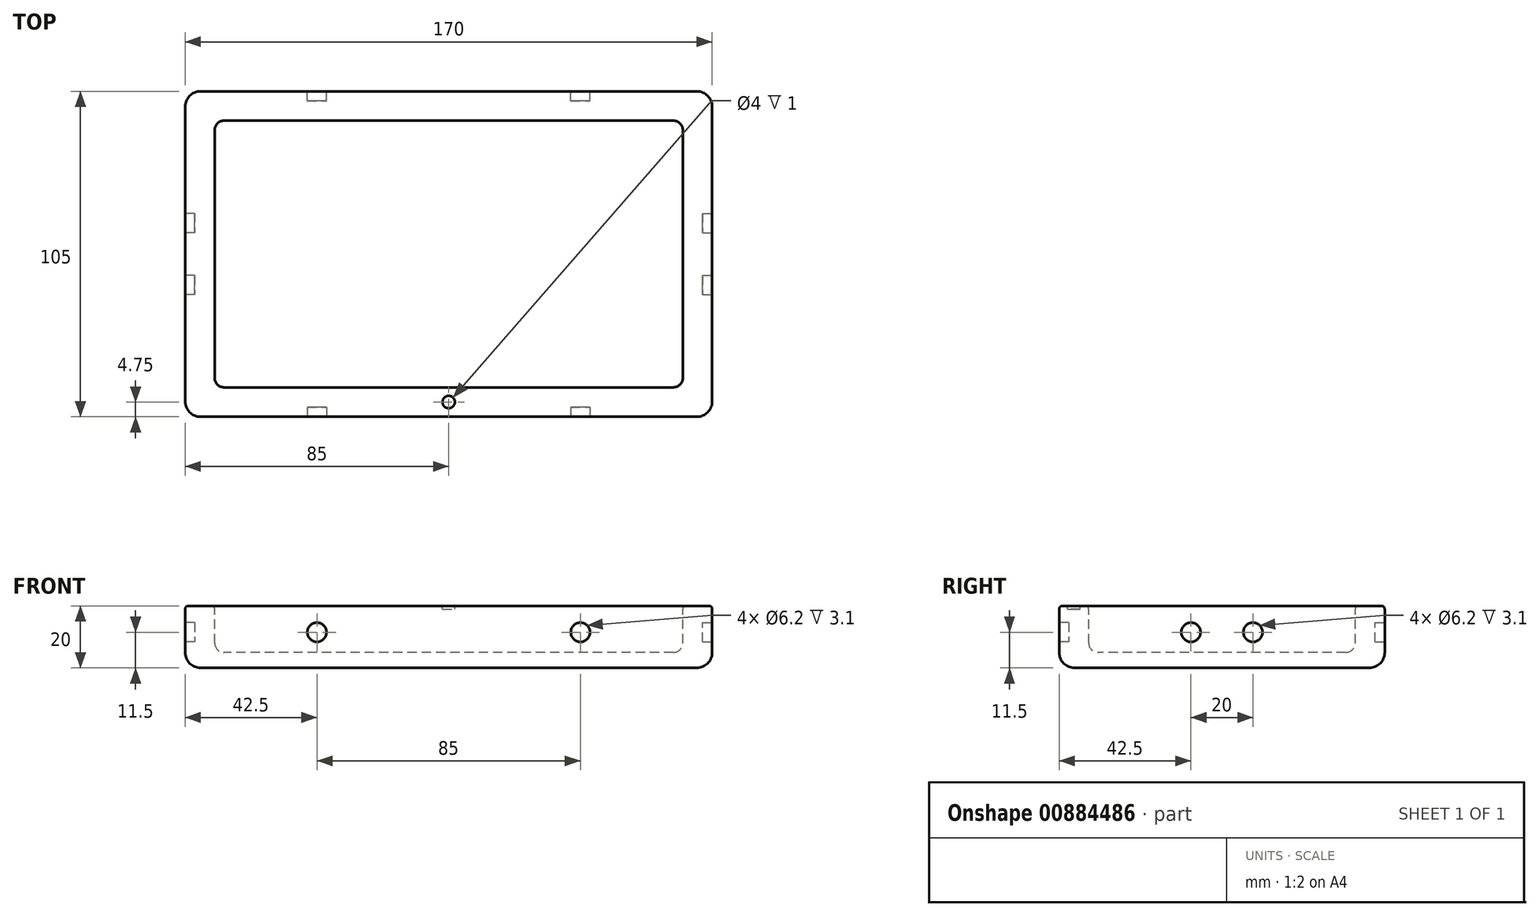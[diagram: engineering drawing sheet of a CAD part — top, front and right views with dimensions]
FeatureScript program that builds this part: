
annotation { "Feature Type Name" : "Feature", "Feature Type Description" : "" }
export const myFeature = defineFeature(function(context is Context, id is Id, definition is map)
    precondition{}
    {
        {
            var Q0;
            Q0=qCreatedBy(makeId("Top.planeOp"),FACE);
            var sketch = newSketch(context, id + "F0", { "sketchPlane" : qUnion([Q0])});
            skLineSegment(sketch, "E0.bottom", {"start": v(-85, 52.5) * mm, "end": v(85, 52.5) * mm});
            skLineSegment(sketch, "E0.top", {"start": v(-85, -52.5) * mm, "end": v(85, -52.5) * mm});
            skLineSegment(sketch, "E0.left", {"start": v(-85, 52.5) * mm, "end": v(-85, -52.5) * mm});
            skLineSegment(sketch, "E0.right", {"start": v(85, 52.5) * mm, "end": v(85, -52.5) * mm});
            skLineSegment(sketch, "E1.bottom", {"start": v(-72.5, 43) * mm, "end": v(72.5, 43) * mm});
            skLineSegment(sketch, "E1.top", {"start": v(-72.5, -43) * mm, "end": v(72.5, -43) * mm});
            skLineSegment(sketch, "E1.left", {"start": v(-75.5, 40) * mm, "end": v(-75.5, -40) * mm});
            skLineSegment(sketch, "E1.right", {"start": v(75.5, 40) * mm, "end": v(75.5, -40) * mm});
            skLineSegment(sketch, "E2.direction1", {"start": v(-75.5, -43) * mm, "end": v(15.26, -43) * mm, "construction": true});
            skPoint(sketch, "E3.visualSharp", {"position": v(-75.5, 43) * mm});
            skArc(sketch, "E3.filletArc", {"start": v(-72.5, 43) * mm, "mid": v(-74.62, 42.12) * mm, "end": v(-75.5, 40) * mm});
            skPoint(sketch, "E4.visualSharp", {"position": v(75.5, 43) * mm});
            skArc(sketch, "E4.filletArc", {"start": v(75.5, 40) * mm, "mid": v(74.62, 42.12) * mm, "end": v(72.5, 43) * mm});
            skPoint(sketch, "E5.visualSharp", {"position": v(75.5, -43) * mm});
            skArc(sketch, "E5.filletArc", {"start": v(72.5, -43) * mm, "mid": v(74.62, -42.12) * mm, "end": v(75.5, -40) * mm});
            skPoint(sketch, "E6.visualSharp", {"position": v(-75.5, -43) * mm});
            skArc(sketch, "E6.filletArc", {"start": v(-75.5, -40) * mm, "mid": v(-74.62, -42.12) * mm, "end": v(-72.5, -43) * mm});
            skLineSegment(sketch, "E7.direction1", {"start": v(-75.5, -43) * mm, "end": v(17, -43) * mm, "construction": true});
            skLineSegment(sketch, "E8", {"start": v(-85, 0) * mm, "end": v(85, 0) * mm, "construction": true});
            skLineSegment(sketch, "E9", {"start": v(0, -52.5) * mm, "end": v(0, 52.5) * mm, "construction": true});
            skCircle(sketch, "E10", {"center": v(0, -47.75) * mm, "radius": 2 * mm});
            skSolve(sketch);
        }
        {
            assignVariable(context, id + "F1", {"name" : "h", "anyValue" : 20});
        }
        {
            assignVariable(context, id + "F2", {"name" : "d", "anyValue" : 15});
        }
        {
            var Q0;
            Q0=makeQuery(id+"F0.imprint","IMPRINT",FACE,{"disambiguationData":[TD([[makeQuery(id+"F0.imprint","IMPRINT",EDGE,{"derivedFrom":sQuery(id+"F0.wireOp",EDGE,"E1.bottom")}),-1.0]])]});
            var Q1;
            Q1=makeQuery(id+"F0.imprint","IMPRINT",FACE,{"disambiguationData":[TD([[makeQuery(id+"F0.imprint","IMPRINT",EDGE,{"derivedFrom":sQuery(id+"F0.wireOp",EDGE,"E0.bottom")}),-1.0]])]});
            var Q2;
            Q2=makeQuery(id+"F0.imprint","IMPRINT",FACE,{"disambiguationData":[TD([[makeQuery(id+"F0.imprint","IMPRINT",EDGE,{"derivedFrom":sQuery(id+"F0.wireOp",EDGE,"E2.0.2.0")}),1.0]])]});
            var Q3;
            Q3=makeQuery(id+"F0.imprint","IMPRINT",FACE,{"disambiguationData":[TD([[makeQuery(id+"F0.imprint","IMPRINT",EDGE,{"derivedFrom":sQuery(id+"F0.wireOp",EDGE,"E2.0.3.0")}),1.0]])]});
            var Q4;
            Q4=makeQuery(id+"F0.imprint","IMPRINT",FACE,{"disambiguationData":[TD([[makeQuery(id+"F0.imprint","IMPRINT",EDGE,{"derivedFrom":sQuery(id+"F0.wireOp",EDGE,"E2.0.1.0")}),1.0]])]});
            var Q5;
            Q5=makeQuery(id+"F0.imprint","IMPRINT",FACE,{"disambiguationData":[TD([[makeQuery(id+"F0.imprint","IMPRINT",EDGE,{"derivedFrom":sQuery(id+"F0.wireOp",EDGE,"E7.0.1.2")}),1.0]])]});
            var Q6;
            Q6=makeQuery(id+"F0.imprint","IMPRINT",FACE,{"disambiguationData":[TD([[makeQuery(id+"F0.imprint","IMPRINT",EDGE,{"derivedFrom":sQuery(id+"F0.wireOp",EDGE,"E7.0.2.2")}),1.0]])]});
            var Q7;
            Q7=makeQuery(id+"F0.imprint","IMPRINT",FACE,{"disambiguationData":[TD([[makeQuery(id+"F0.imprint","IMPRINT",EDGE,{"derivedFrom":sQuery(id+"F0.wireOp",EDGE,"E7.0.3.2")}),1.0]])]});
            var Q8;
            Q8=makeQuery(id+"F0.imprint","IMPRINT",FACE,{"disambiguationData":[TD([[makeQuery(id+"F0.imprint","IMPRINT",EDGE,{"derivedFrom":sQuery(id+"F0.wireOp",EDGE,"E10")}),1.0]])]});
            extrude(context, id + "F3", {"entities" : qUnion([Q0, Q1, Q2, Q3, Q4, Q5, Q6, Q7, Q8]), "depth" : (getVariable(context, 'h')) * mm, "offsetDistance" : 25 * mm});
        }
        {
            var Q0;
            Q0=makeQuery(id+"F0.imprint","IMPRINT",FACE,{"disambiguationData":[TD([[makeQuery(id+"F0.imprint","IMPRINT",EDGE,{"derivedFrom":sQuery(id+"F0.wireOp",EDGE,"E1.bottom")}),-1.0]])]});
            var Q1;
            Q1=makeQuery(id+"F0.imprint","IMPRINT",FACE,{"disambiguationData":[TD([[makeQuery(id+"F0.imprint","IMPRINT",EDGE,{"derivedFrom":sQuery(id+"F0.wireOp",EDGE,"E2.0.1.0")}),1.0]])]});
            var Q2;
            Q2=makeQuery(id+"F0.imprint","IMPRINT",FACE,{"disambiguationData":[TD([[makeQuery(id+"F0.imprint","IMPRINT",EDGE,{"derivedFrom":sQuery(id+"F0.wireOp",EDGE,"E2.0.2.0")}),1.0]])]});
            var Q3;
            Q3=makeQuery(id+"F0.imprint","IMPRINT",FACE,{"disambiguationData":[TD([[makeQuery(id+"F0.imprint","IMPRINT",EDGE,{"derivedFrom":sQuery(id+"F0.wireOp",EDGE,"E2.0.3.0")}),1.0]])]});
            var Q4;
            Q4=makeQuery(id+"F0.imprint","IMPRINT",FACE,{"disambiguationData":[TD([[makeQuery(id+"F0.imprint","IMPRINT",EDGE,{"derivedFrom":sQuery(id+"F0.wireOp",EDGE,"E7.0.1.2")}),1.0]])]});
            var Q5;
            Q5=makeQuery(id+"F0.imprint","IMPRINT",FACE,{"disambiguationData":[TD([[makeQuery(id+"F0.imprint","IMPRINT",EDGE,{"derivedFrom":sQuery(id+"F0.wireOp",EDGE,"E7.0.2.2")}),1.0]])]});
            var Q6;
            Q6=makeQuery(id+"F0.imprint","IMPRINT",FACE,{"disambiguationData":[TD([[makeQuery(id+"F0.imprint","IMPRINT",EDGE,{"derivedFrom":sQuery(id+"F0.wireOp",EDGE,"E7.0.3.2")}),1.0]])]});
            extrude(context, id + "F4", {"entities" : qUnion([Q0, Q1, Q2, Q3, Q4, Q5, Q6]), "operationType" : NewBodyOperationType.REMOVE, "depth" : (getVariable(context, 'd')) * mm, "offsetDistance" : 25 * mm});
        }
        {
            var Q0;
            Q0=makeQuery(id+"F3.opExtrude","CAP_FACE",FACE,{"disambiguationData":[OSD([sQuery(id+"F0.wireOp",EDGE,"E0.bottom"),sQuery(id+"F0.wireOp",EDGE,"E0.top"),sQuery(id+"F0.wireOp",EDGE,"E0.left"),sQuery(id+"F0.wireOp",EDGE,"E0.right")])],"isStart":false});
            var Q1;
            Q1=makeQuery(id+"F3.opExtrude","SWEPT_EDGE",EDGE,{"disambiguationData":[OSD([sQuery(id+"F0.wireOp",EDGE,"E0.bottom"),sQuery(id+"F0.wireOp",EDGE,"E0.right")])]});
            var Q2;
            Q2=makeQuery(id+"F3.opExtrude","SWEPT_EDGE",EDGE,{"disambiguationData":[OSD([sQuery(id+"F0.wireOp",EDGE,"E0.bottom"),sQuery(id+"F0.wireOp",EDGE,"E0.left")])]});
            var Q3;
            Q3=makeQuery(id+"F3.opExtrude","SWEPT_EDGE",EDGE,{"disambiguationData":[OSD([sQuery(id+"F0.wireOp",EDGE,"E0.top"),sQuery(id+"F0.wireOp",EDGE,"E0.left")])]});
            var Q4;
            Q4=makeQuery(id+"F3.opExtrude","SWEPT_EDGE",EDGE,{"disambiguationData":[OSD([sQuery(id+"F0.wireOp",EDGE,"E0.top"),sQuery(id+"F0.wireOp",EDGE,"E0.right")])]});
            fillet(context, id + "F5", {"entities" : qUnion([Q0, Q1, Q2, Q3, Q4]), "radius" : 5 * mm, "tangentPropagation" : true, "allowEdgeOverflow" : false});
        }
        {
            var Q0;
            Q0=makeQuery(id+"F4.boolean.opBoolean","COPY",FACE,{"derivedFrom":makeQuery(id+"F4.opExtrude","CAP_FACE",FACE,{"disambiguationData":[OSD([sQuery(id+"F0.wireOp",EDGE,"E1.bottom"),sQuery(id+"F0.wireOp",EDGE,"E1.top"),sQuery(id+"F0.wireOp",EDGE,"E1.left"),sQuery(id+"F0.wireOp",EDGE,"E1.right"),sQuery(id+"F0.wireOp",EDGE,"E3.filletArc"),sQuery(id+"F0.wireOp",EDGE,"E4.filletArc"),sQuery(id+"F0.wireOp",EDGE,"E5.filletArc"),sQuery(id+"F0.wireOp",EDGE,"E6.filletArc")])],"isStart":false})});
            var Q1;
            Q1=makeQuery(id+"F4.boolean.opBoolean","COPY",FACE,{"derivedFrom":makeQuery(id+"F4.opExtrude","CAP_FACE",FACE,{"disambiguationData":[OSD([sQuery(id+"F0.wireOp",EDGE,"E7.0.1.2"),sQuery(id+"F0.wireOp",EDGE,"E7.0.1.4"),sQuery(id+"F0.wireOp",EDGE,"E7.0.1.5"),sQuery(id+"F0.wireOp",EDGE,"E7.0.1.6"),sQuery(id+"F0.wireOp",EDGE,"E7.0.1.7"),sQuery(id+"F0.wireOp",EDGE,"E7.0.1.9"),sQuery(id+"F0.wireOp",EDGE,"E7.0.1.11"),sQuery(id+"F0.wireOp",EDGE,"E7.0.1.12")])],"isStart":false})});
            var Q2;
            Q2=makeQuery(id+"F4.boolean.opBoolean","COPY",FACE,{"derivedFrom":makeQuery(id+"F4.opExtrude","CAP_FACE",FACE,{"disambiguationData":[OSD([sQuery(id+"F0.wireOp",EDGE,"E7.0.2.2"),sQuery(id+"F0.wireOp",EDGE,"E7.0.2.4"),sQuery(id+"F0.wireOp",EDGE,"E7.0.2.5"),sQuery(id+"F0.wireOp",EDGE,"E7.0.2.6"),sQuery(id+"F0.wireOp",EDGE,"E7.0.2.7"),sQuery(id+"F0.wireOp",EDGE,"E7.0.2.9"),sQuery(id+"F0.wireOp",EDGE,"E7.0.2.11"),sQuery(id+"F0.wireOp",EDGE,"E7.0.2.12")])],"isStart":false})});
            var Q3;
            Q3=makeQuery(id+"F4.boolean.opBoolean","COPY",FACE,{"derivedFrom":makeQuery(id+"F4.opExtrude","CAP_FACE",FACE,{"disambiguationData":[OSD([sQuery(id+"F0.wireOp",EDGE,"E7.0.3.2"),sQuery(id+"F0.wireOp",EDGE,"E7.0.3.4"),sQuery(id+"F0.wireOp",EDGE,"E7.0.3.5"),sQuery(id+"F0.wireOp",EDGE,"E7.0.3.6"),sQuery(id+"F0.wireOp",EDGE,"E7.0.3.7"),sQuery(id+"F0.wireOp",EDGE,"E7.0.3.9"),sQuery(id+"F0.wireOp",EDGE,"E7.0.3.11"),sQuery(id+"F0.wireOp",EDGE,"E7.0.3.12")])],"isStart":false})});
            fillet(context, id + "F6", {"entities" : qUnion([Q0, Q1, Q2, Q3]), "radius" : 3 * mm, "tangentPropagation" : true, "allowEdgeOverflow" : false});
        }
        {
            var Q0;
            Q0=makeQuery(id+"F3.opExtrude","CAP_FACE",FACE,{"disambiguationData":[OSD([sQuery(id+"F0.wireOp",EDGE,"E0.bottom"),sQuery(id+"F0.wireOp",EDGE,"E0.top"),sQuery(id+"F0.wireOp",EDGE,"E0.left"),sQuery(id+"F0.wireOp",EDGE,"E0.right")])],"isStart":true});
            fillet(context, id + "F7", {"entities" : qUnion([Q0]), "radius" : 1 * mm, "tangentPropagation" : true, "allowEdgeOverflow" : false});
        }
        {
            var Q0;
            Q0=makeQuery(id+"F3.opExtrude","SWEPT_FACE",FACE,{"disambiguationData":[OSD([sQuery(id+"F0.wireOp",EDGE,"E0.top")])]});
            var sketch = newSketch(context, id + "F8", { "sketchPlane" : qUnion([Q0])});
            skCircle(sketch, "E11", {"center": v(42.5, 8.5) * mm, "radius": 3.1 * mm});
            skCircle(sketch, "E12", {"center": v(-42.5, 8.5) * mm, "radius": 3.1 * mm});
            skLineSegment(sketch, "E13", {"start": v(-42.5, 8.5) * mm, "end": v(42.5, 8.5) * mm, "construction": true});
            skSolve(sketch);
        }
        {
            var Q0;
            Q0=makeQuery(id+"F8.imprint","IMPRINT",FACE,{"disambiguationData":[TD([[makeQuery(id+"F8.imprint","IMPRINT",EDGE,{"derivedFrom":sQuery(id+"F8.wireOp",EDGE,"E11")}),1.0]])]});
            var Q1;
            Q1=makeQuery(id+"F8.imprint","IMPRINT",FACE,{"disambiguationData":[TD([[makeQuery(id+"F8.imprint","IMPRINT",EDGE,{"derivedFrom":sQuery(id+"F8.wireOp",EDGE,"E12")}),1.0]])]});
            extrude(context, id + "F9", {"entities" : qUnion([Q0, Q1]), "operationType" : NewBodyOperationType.REMOVE, "oppositeDirection" : true, "depth" : 3.1 * mm, "offsetDistance" : 25 * mm});
        }
        {
            var Q0;
            Q0=makeQuery(id+"F3.opExtrude","SWEPT_FACE",FACE,{"disambiguationData":[OSD([sQuery(id+"F0.wireOp",EDGE,"E0.bottom")])]});
            var sketch = newSketch(context, id + "F10", { "sketchPlane" : qUnion([Q0])});
            skCircle(sketch, "E14", {"center": v(42.5, 8.5) * mm, "radius": 3.1 * mm});
            skCircle(sketch, "E15", {"center": v(-42.5, 8.5) * mm, "radius": 3.1 * mm});
            skLineSegment(sketch, "E16", {"start": v(42.5, 8.5) * mm, "end": v(-42.5, 8.5) * mm, "construction": true});
            skSolve(sketch);
        }
        {
            var Q0;
            Q0=makeQuery(id+"F10.imprint","IMPRINT",FACE,{"disambiguationData":[TD([[makeQuery(id+"F10.imprint","IMPRINT",EDGE,{"derivedFrom":sQuery(id+"F10.wireOp",EDGE,"E14")}),1.0]])]});
            var Q1;
            Q1=makeQuery(id+"F10.imprint","IMPRINT",FACE,{"disambiguationData":[TD([[makeQuery(id+"F10.imprint","IMPRINT",EDGE,{"derivedFrom":sQuery(id+"F10.wireOp",EDGE,"E15")}),1.0]])]});
            extrude(context, id + "F11", {"entities" : qUnion([Q0, Q1]), "operationType" : NewBodyOperationType.REMOVE, "oppositeDirection" : true, "depth" : 3.1 * mm, "offsetDistance" : 25 * mm});
        }
        {
            var Q0;
            Q0=makeQuery(id+"F3.opExtrude","SWEPT_FACE",FACE,{"disambiguationData":[OSD([sQuery(id+"F0.wireOp",EDGE,"E0.left")])]});
            var sketch = newSketch(context, id + "F12", { "sketchPlane" : qUnion([Q0])});
            skCircle(sketch, "E17", {"center": v(10, 8.5) * mm, "radius": 3.1 * mm});
            skCircle(sketch, "E18", {"center": v(-10, 8.5) * mm, "radius": 3.1 * mm});
            skLineSegment(sketch, "E19", {"start": v(-10, 8.5) * mm, "end": v(10, 8.5) * mm, "construction": true});
            skSolve(sketch);
        }
        {
            var Q0;
            Q0=makeQuery(id+"F12.imprint","IMPRINT",FACE,{"disambiguationData":[TD([[makeQuery(id+"F12.imprint","IMPRINT",EDGE,{"derivedFrom":sQuery(id+"F12.wireOp",EDGE,"E17")}),1.0]])]});
            var Q1;
            Q1=makeQuery(id+"F12.imprint","IMPRINT",FACE,{"disambiguationData":[TD([[makeQuery(id+"F12.imprint","IMPRINT",EDGE,{"derivedFrom":sQuery(id+"F12.wireOp",EDGE,"E18")}),1.0]])]});
            extrude(context, id + "F13", {"entities" : qUnion([Q0, Q1]), "operationType" : NewBodyOperationType.REMOVE, "oppositeDirection" : true, "depth" : 3.1 * mm, "offsetDistance" : 25 * mm});
        }
        {
            var Q0;
            Q0=makeQuery(id+"F3.opExtrude","SWEPT_FACE",FACE,{"disambiguationData":[OSD([sQuery(id+"F0.wireOp",EDGE,"E0.right")])]});
            var sketch = newSketch(context, id + "F14", { "sketchPlane" : qUnion([Q0])});
            skCircle(sketch, "E20", {"center": v(10, 8.5) * mm, "radius": 3.1 * mm});
            skCircle(sketch, "E21", {"center": v(-10, 8.5) * mm, "radius": 3.1 * mm});
            skLineSegment(sketch, "E22", {"start": v(10, 8.5) * mm, "end": v(-10, 8.5) * mm, "construction": true});
            skSolve(sketch);
        }
        {
            var Q0;
            Q0=makeQuery(id+"F14.imprint","IMPRINT",FACE,{"disambiguationData":[TD([[makeQuery(id+"F14.imprint","IMPRINT",EDGE,{"derivedFrom":sQuery(id+"F14.wireOp",EDGE,"E20")}),1.0]])]});
            var Q1;
            Q1=makeQuery(id+"F14.imprint","IMPRINT",FACE,{"disambiguationData":[TD([[makeQuery(id+"F14.imprint","IMPRINT",EDGE,{"derivedFrom":sQuery(id+"F14.wireOp",EDGE,"E21")}),1.0]])]});
            extrude(context, id + "F15", {"entities" : qUnion([Q0, Q1]), "operationType" : NewBodyOperationType.REMOVE, "oppositeDirection" : true, "depth" : 3.1 * mm, "offsetDistance" : 25 * mm});
        }
        {
            var Q0;
            Q0=makeQuery(id+"F0.imprint","IMPRINT",FACE,{"disambiguationData":[TD([[makeQuery(id+"F0.imprint","IMPRINT",EDGE,{"derivedFrom":sQuery(id+"F0.wireOp",EDGE,"E10")}),1.0]])]});
            var Q1;
            Q1=sQuery(id+"F0.wireOp",EDGE,"E10");
            extrude(context, id + "F16", {"entities" : qUnion([Q0]), "operationType" : NewBodyOperationType.REMOVE, "surfaceEntities" : qUnion([Q1]), "depth" : 1 * mm, "offsetDistance" : 25 * mm});
        }
        {
            var Q0;
            Q0=makeQuery(id+"F3.opExtrude","SWEPT_BODY",BODY,{"disambiguationData":[OSD([sQuery(id+"F0.wireOp",EDGE,"E0.bottom"),sQuery(id+"F0.wireOp",EDGE,"E0.top"),sQuery(id+"F0.wireOp",EDGE,"E0.left"),sQuery(id+"F0.wireOp",EDGE,"E0.right")])]});
            var Q1;
            Q1=sQuery(id+"F0.wireOp",EDGE,"E9");
            transform(context, id + "F17", {"entities" : qUnion([Q0]), "transformType" : TransformType.ROTATION, "transformAxis" : qUnion([Q1]), "angle" : 180 * degree, "makeCopy" : false});
        }
    });
